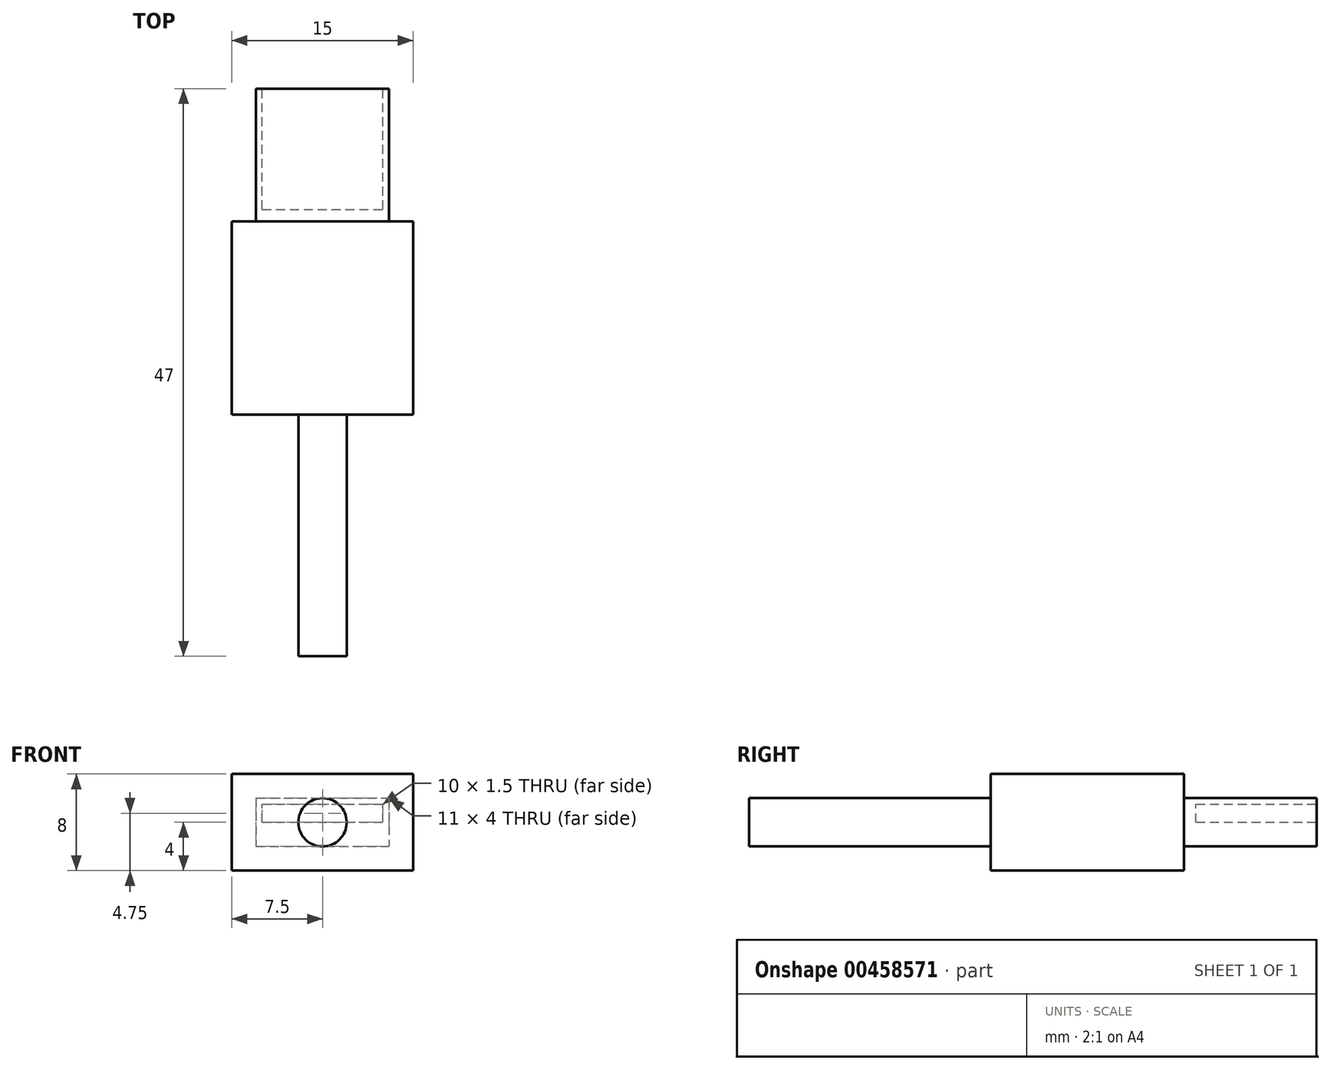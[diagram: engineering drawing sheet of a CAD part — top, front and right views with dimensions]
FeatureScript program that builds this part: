
annotation { "Feature Type Name" : "Feature", "Feature Type Description" : "" }
export const myFeature = defineFeature(function(context is Context, id is Id, definition is map)
    precondition{}
    {
        {
            var Q0;
            Q0=qCreatedBy(makeId("Front.planeOp"),FACE);
            var sketch = newSketch(context, id + "F0", { "sketchPlane" : qUnion([Q0])});
            skLineSegment(sketch, "E0.bottom", {"start": v(-5.5, 2) * mm, "end": v(5.5, 2) * mm});
            skLineSegment(sketch, "E0.top", {"start": v(-5.5, -2) * mm, "end": v(5.5, -2) * mm});
            skLineSegment(sketch, "E0.left", {"start": v(-5.5, 2) * mm, "end": v(-5.5, -2) * mm});
            skLineSegment(sketch, "E0.right", {"start": v(5.5, 2) * mm, "end": v(5.5, -2) * mm});
            skPoint(sketch, "E0.middle", {"position": v(0, 0) * mm});
            skSolve(sketch);
        }
        {
            var Q0;
            Q0 = qSketchRegion(id + "F0", true);
            extrude(context, id + "F1", {"entities" : qUnion([Q0]), "depth" : 11 * mm, "offsetDistance" : 25 * mm});
        }
        {
            var Q0;
            Q0=makeQuery(id+"F1.opExtrude","CAP_FACE",FACE,{"disambiguationData":[OSD([sQuery(id+"F0.wireOp",EDGE,"E0.bottom"),sQuery(id+"F0.wireOp",EDGE,"E0.top"),sQuery(id+"F0.wireOp",EDGE,"E0.left"),sQuery(id+"F0.wireOp",EDGE,"E0.right")])],"isStart":false});
            var sketch = newSketch(context, id + "F2", { "sketchPlane" : qUnion([Q0])});
            skLineSegment(sketch, "E1.bottom", {"start": v(-7.5, 4) * mm, "end": v(7.5, 4) * mm});
            skLineSegment(sketch, "E1.top", {"start": v(-7.5, -4) * mm, "end": v(7.5, -4) * mm});
            skLineSegment(sketch, "E1.left", {"start": v(-7.5, 4) * mm, "end": v(-7.5, -4) * mm});
            skLineSegment(sketch, "E1.right", {"start": v(7.5, 4) * mm, "end": v(7.5, -4) * mm});
            skSolve(sketch);
        }
        {
            var Q0;
            Q0 = qSketchRegion(id + "F2", true);
            extrude(context, id + "F3", {"entities" : qUnion([Q0]), "operationType" : NewBodyOperationType.ADD, "depth" : 16 * mm, "offsetDistance" : 25 * mm});
        }
        {
            var Q0;
            Q0=makeQuery(id+"F3.opExtrude","CAP_FACE",FACE,{"disambiguationData":[OSD([sQuery(id+"F2.wireOp",EDGE,"E1.bottom"),sQuery(id+"F2.wireOp",EDGE,"E1.top"),sQuery(id+"F2.wireOp",EDGE,"E1.left"),sQuery(id+"F2.wireOp",EDGE,"E1.right")])],"isStart":false});
            var sketch = newSketch(context, id + "F4", { "sketchPlane" : qUnion([Q0])});
            skCircle(sketch, "E2", {"center": v(0, 0) * mm, "radius": 2 * mm});
            skSolve(sketch);
        }
        {
            var Q0;
            Q0 = qSketchRegion(id + "F4", true);
            extrude(context, id + "F5", {"entities" : qUnion([Q0]), "operationType" : NewBodyOperationType.ADD, "depth" : 20 * mm, "offsetDistance" : 25 * mm});
        }
        {
            var Q0;
            Q0=makeQuery(id+"F1.opExtrude","CAP_FACE",FACE,{"disambiguationData":[OSD([sQuery(id+"F0.wireOp",EDGE,"E0.bottom"),sQuery(id+"F0.wireOp",EDGE,"E0.top"),sQuery(id+"F0.wireOp",EDGE,"E0.left"),sQuery(id+"F0.wireOp",EDGE,"E0.right")])],"isStart":true});
            var sketch = newSketch(context, id + "F6", { "sketchPlane" : qUnion([Q0])});
            skLineSegment(sketch, "E3.bottom", {"start": v(5, 0) * mm, "end": v(-5, 0) * mm});
            skLineSegment(sketch, "E3.top", {"start": v(5, 1.5) * mm, "end": v(-5, 1.5) * mm});
            skLineSegment(sketch, "E3.left", {"start": v(5, 0) * mm, "end": v(5, 1.5) * mm});
            skLineSegment(sketch, "E3.right", {"start": v(-5, 0) * mm, "end": v(-5, 1.5) * mm});
            skSolve(sketch);
        }
        {
            var Q0;
            Q0 = qSketchRegion(id + "F6", true);
            extrude(context, id + "F7", {"entities" : qUnion([Q0]), "operationType" : NewBodyOperationType.REMOVE, "oppositeDirection" : true, "depth" : 10 * mm, "offsetDistance" : 25 * mm});
        }
        {
            var Q0;
            Q0=makeQuery(id+"F1.opExtrude","SWEPT_BODY",BODY,{"disambiguationData":[OSD([sQuery(id+"F0.wireOp",EDGE,"E0.bottom"),sQuery(id+"F0.wireOp",EDGE,"E0.top"),sQuery(id+"F0.wireOp",EDGE,"E0.left"),sQuery(id+"F0.wireOp",EDGE,"E0.right")])]});
            transform(context, id + "F8", {"entities" : qUnion([Q0]), "transformType" : TransformType.TRANSLATION_3D, "dx" : 0 * mm, "dy" : 0 * mm, "dz" : 0 * mm, "makeCopy" : true});
        }
    });
